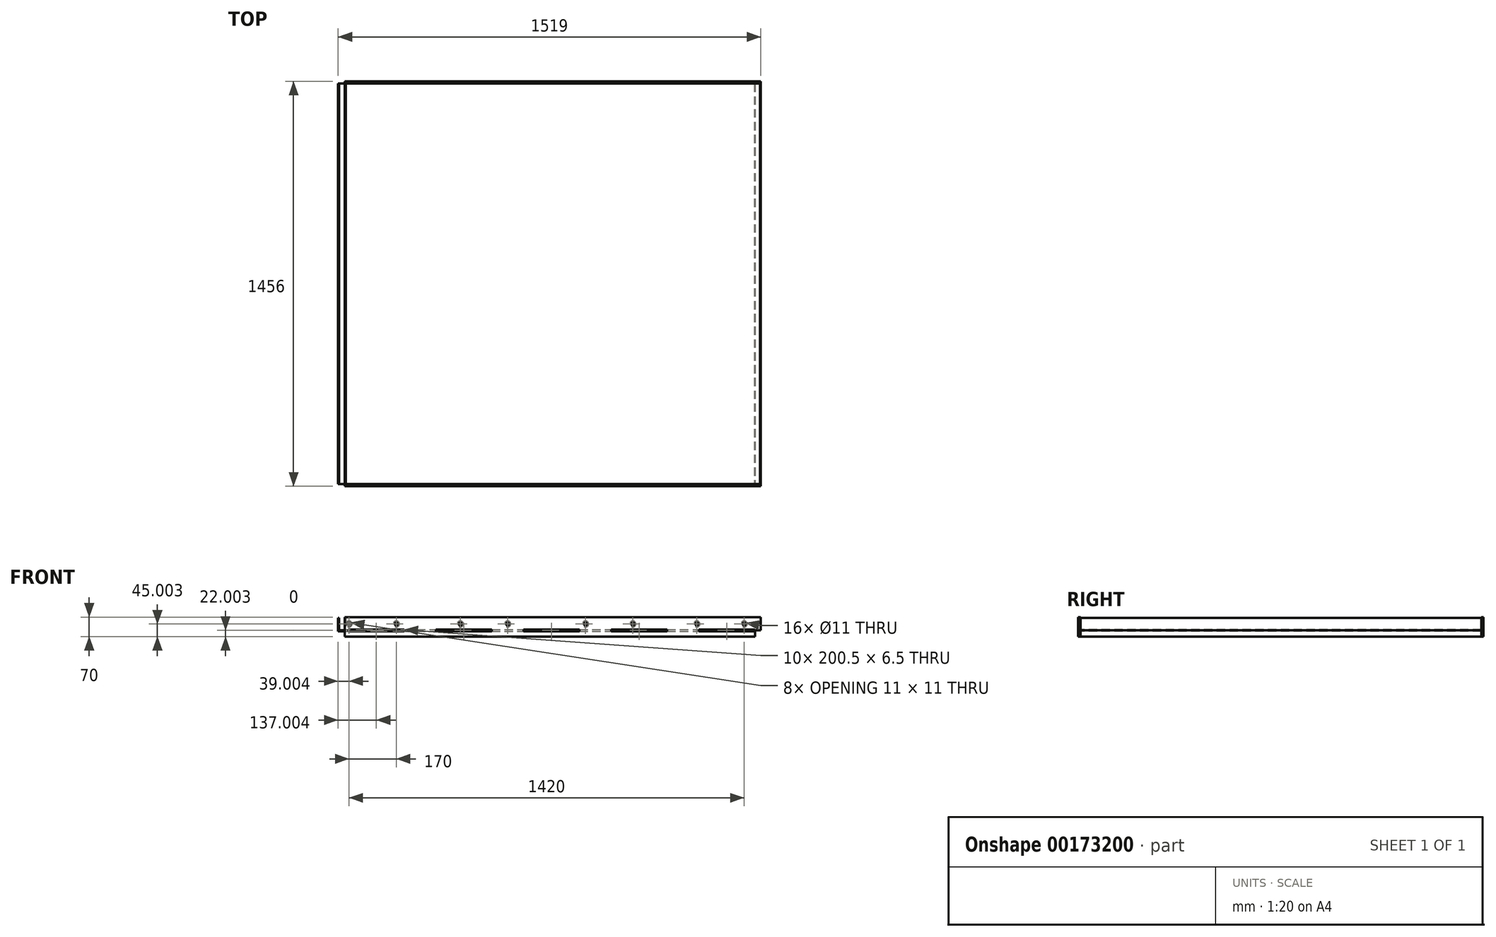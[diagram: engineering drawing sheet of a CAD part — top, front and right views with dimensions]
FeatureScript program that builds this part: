
annotation { "Feature Type Name" : "Feature", "Feature Type Description" : "" }
export const myFeature = defineFeature(function(context is Context, id is Id, definition is map)
    precondition{}
    {
        {
            var Q0;
            Q0=qCreatedBy(makeId("Front.planeOp"),FACE);
            var sketch = newSketch(context, id + "F0", { "sketchPlane" : qUnion([Q0])});
            skLineSegment(sketch, "E0", {"start": v(-1403.49, 88.26) * mm, "end": v(-1403.49, 40.26) * mm});
            skLineSegment(sketch, "E1", {"start": v(-1403.49, 40.26) * mm, "end": v(91.51, 40.26) * mm});
            skLineSegment(sketch, "E2", {"start": v(91.51, 40.26) * mm, "end": v(91.51, 21.26) * mm});
            skLineSegment(sketch, "E3", {"start": v(91.51, 21.26) * mm, "end": v(94.51, 21.26) * mm});
            skLineSegment(sketch, "E4", {"start": v(94.51, 21.26) * mm, "end": v(94.51, 43.26) * mm});
            skLineSegment(sketch, "E5", {"start": v(94.51, 43.26) * mm, "end": v(-1400.49, 43.26) * mm});
            skLineSegment(sketch, "E6", {"start": v(-1400.49, 43.26) * mm, "end": v(-1400.49, 88.26) * mm});
            skLineSegment(sketch, "E7", {"start": v(-1400.49, 88.26) * mm, "end": v(-1403.49, 88.26) * mm});
            skLineSegment(sketch, "E8", {"start": v(-1379.49, 43.26) * mm, "end": v(-1379.49, 88.26) * mm});
            skLineSegment(sketch, "E9", {"start": v(-1379.49, 88.26) * mm, "end": v(-1376.49, 88.26) * mm});
            skLineSegment(sketch, "E10", {"start": v(-1376.49, 88.26) * mm, "end": v(-1376.49, 46.26) * mm});
            skLineSegment(sketch, "E11", {"start": v(-1376.49, 46.26) * mm, "end": v(112.51, 46.26) * mm});
            skLineSegment(sketch, "E12", {"start": v(115.51, 46.26) * mm, "end": v(115.51, 43.26) * mm});
            skLineSegment(sketch, "E13", {"start": v(-1379.49, 43.26) * mm, "end": v(115.51, 43.26) * mm});
            skLineSegment(sketch, "E14", {"start": v(115.51, 46.26) * mm, "end": v(115.51, 88.26) * mm});
            skLineSegment(sketch, "E15", {"start": v(115.51, 88.26) * mm, "end": v(112.51, 88.26) * mm});
            skLineSegment(sketch, "E16", {"start": v(112.51, 88.26) * mm, "end": v(112.51, 46.26) * mm});
            skLineSegment(sketch, "E17.bottom", {"start": v(-1397.49, 82.67) * mm, "end": v(-1382.49, 82.67) * mm, "construction": true});
            skLineSegment(sketch, "E17.top", {"start": v(-1397.49, 47.75) * mm, "end": v(-1382.49, 47.75) * mm, "construction": true});
            skLineSegment(sketch, "E17.left", {"start": v(-1397.49, 82.67) * mm, "end": v(-1397.49, 47.75) * mm, "construction": true});
            skLineSegment(sketch, "E17.right", {"start": v(-1382.49, 82.67) * mm, "end": v(-1382.49, 47.75) * mm, "construction": true});
            skSolve(sketch);
        }
        {
            var Q0;
            Q0=makeQuery(id+"F0.imprint","IMPRINT",FACE,{"disambiguationData":[TD([[makeQuery(id+"F0.imprint","IMPRINT",EDGE,{"derivedFrom":sQuery(id+"F0.wireOp",EDGE,"E0")}),1.0]])]});
            extrude(context, id + "F1", {"entities" : qUnion([Q0]), "oppositeDirection" : true, "depth" : 1440 * mm});
        }
        {
            var Q0;
            {var subQ0=sQuery(id+"F0.wireOp",EDGE,"E8");Q0=makeQuery(id+"F0.imprint","IMPRINT",FACE,{"disambiguationData":[TD([[makeQuery(id+"F0.imprint","IMPRINT",EDGE,{"derivedFrom":subQ0}),-1.0]])]});}
            extrude(context, id + "F2", {"entities" : qUnion([Q0]), "oppositeDirection" : true, "depth" : 1440 * mm});
        }
        {
            var Q0;
            Q0=makeQuery(id+"F1.opExtrude","SWEPT_FACE",FACE,{"disambiguationData":[OSD([sQuery(id+"F0.wireOp",EDGE,"E5"),sQuery(id+"F0.wireOp",EDGE,"E13")])]});
            var sketch = newSketch(context, id + "F3", { "sketchPlane" : qUnion([Q0])});
            skLineSegment(sketch, "E18.bottom", {"start": v(-1366.49, 0) * mm, "end": v(-1166.49, 0) * mm});
            skLineSegment(sketch, "E18.top", {"start": v(-1366.49, -7) * mm, "end": v(-1166.49, -7) * mm});
            skLineSegment(sketch, "E18.left", {"start": v(-1366.49, 0) * mm, "end": v(-1366.49, -7) * mm});
            skLineSegment(sketch, "E18.right", {"start": v(-1166.49, 0) * mm, "end": v(-1166.49, -7) * mm});
            skLineSegment(sketch, "E19.1.0.0", {"start": v(-1051.49, 0) * mm, "end": v(-851.49, 0) * mm});
            skLineSegment(sketch, "E19.1.0.1", {"start": v(-1051.49, -7) * mm, "end": v(-851.49, -7) * mm});
            skLineSegment(sketch, "E19.1.0.2", {"start": v(-851.49, 0) * mm, "end": v(-851.49, -7) * mm});
            skLineSegment(sketch, "E19.1.0.3", {"start": v(-1051.49, 0) * mm, "end": v(-1051.49, -7) * mm});
            skLineSegment(sketch, "E19.2.0.0", {"start": v(-736.49, 0) * mm, "end": v(-536.49, 0) * mm});
            skLineSegment(sketch, "E19.2.0.1", {"start": v(-736.49, -7) * mm, "end": v(-536.49, -7) * mm});
            skLineSegment(sketch, "E19.2.0.2", {"start": v(-536.49, 0) * mm, "end": v(-536.49, -7) * mm});
            skLineSegment(sketch, "E19.2.0.3", {"start": v(-736.49, 0) * mm, "end": v(-736.49, -7) * mm});
            skLineSegment(sketch, "E19.3.0.0", {"start": v(-421.49, 0) * mm, "end": v(-221.49, 0) * mm});
            skLineSegment(sketch, "E19.3.0.1", {"start": v(-421.49, -7) * mm, "end": v(-221.49, -7) * mm});
            skLineSegment(sketch, "E19.3.0.2", {"start": v(-221.49, 0) * mm, "end": v(-221.49, -7) * mm});
            skLineSegment(sketch, "E19.3.0.3", {"start": v(-421.49, 0) * mm, "end": v(-421.49, -7) * mm});
            skLineSegment(sketch, "E19.4.0.0", {"start": v(-106.49, 0) * mm, "end": v(93.51, 0) * mm});
            skLineSegment(sketch, "E19.4.0.1", {"start": v(-106.49, -7) * mm, "end": v(93.51, -7) * mm});
            skLineSegment(sketch, "E19.4.0.2", {"start": v(93.51, 0) * mm, "end": v(93.51, -7) * mm});
            skLineSegment(sketch, "E19.4.0.3", {"start": v(-106.49, 0) * mm, "end": v(-106.49, -7) * mm});
            skLineSegment(sketch, "E19.direction1", {"start": v(-1366.49, -7) * mm, "end": v(-1051.49, -7) * mm, "construction": true});
            skLineSegment(sketch, "E20", {"start": v(-1400.49, 720) * mm, "end": v(412.72, 720) * mm, "construction": true});
            skLineSegment(sketch, "E21.MirrorCS", {"start": v(-1366.49, 1440) * mm, "end": v(-1366.49, 1447) * mm});
            skLineSegment(sketch, "E22.MirrorCS", {"start": v(-1051.49, 1440) * mm, "end": v(-1051.49, 1447) * mm});
            skLineSegment(sketch, "E23.MirrorCS", {"start": v(-421.49, 1440) * mm, "end": v(-421.49, 1447) * mm});
            skLineSegment(sketch, "E24.MirrorCS", {"start": v(93.51, 1440) * mm, "end": v(93.51, 1447) * mm});
            skLineSegment(sketch, "E25.MirrorCS", {"start": v(-221.49, 1440) * mm, "end": v(-221.49, 1447) * mm});
            skLineSegment(sketch, "E26.MirrorCS", {"start": v(-106.49, 1440) * mm, "end": v(-106.49, 1447) * mm});
            skLineSegment(sketch, "E27.MirrorCS", {"start": v(-736.49, 1440) * mm, "end": v(-736.49, 1447) * mm});
            skLineSegment(sketch, "E28.MirrorCS", {"start": v(-536.49, 1440) * mm, "end": v(-536.49, 1447) * mm});
            skLineSegment(sketch, "E29.MirrorCS", {"start": v(-851.49, 1440) * mm, "end": v(-851.49, 1447) * mm});
            skLineSegment(sketch, "E30.MirrorCS", {"start": v(-1166.49, 1440) * mm, "end": v(-1166.49, 1447) * mm});
            skLineSegment(sketch, "E31.MirrorCS", {"start": v(-1366.49, 1440) * mm, "end": v(-1166.49, 1440) * mm});
            skLineSegment(sketch, "E32.MirrorCS", {"start": v(-106.49, 1447) * mm, "end": v(93.51, 1447) * mm});
            skLineSegment(sketch, "E33.MirrorCS", {"start": v(-421.49, 1440) * mm, "end": v(-221.49, 1440) * mm});
            skLineSegment(sketch, "E34.MirrorCS", {"start": v(-736.49, 1440) * mm, "end": v(-536.49, 1440) * mm});
            skLineSegment(sketch, "E35.MirrorCS", {"start": v(-1366.49, 1447) * mm, "end": v(-1166.49, 1447) * mm});
            skLineSegment(sketch, "E36.MirrorCS", {"start": v(-1051.49, 1440) * mm, "end": v(-851.49, 1440) * mm});
            skLineSegment(sketch, "E37.MirrorCS", {"start": v(-106.49, 1440) * mm, "end": v(93.51, 1440) * mm});
            skLineSegment(sketch, "E38.MirrorCS", {"start": v(-421.49, 1447) * mm, "end": v(-221.49, 1447) * mm});
            skLineSegment(sketch, "E39.MirrorCS", {"start": v(-1366.49, 1447) * mm, "end": v(-1051.49, 1447) * mm, "construction": true});
            skLineSegment(sketch, "E40.MirrorCS", {"start": v(-736.49, 1447) * mm, "end": v(-536.49, 1447) * mm});
            skLineSegment(sketch, "E41.MirrorCS", {"start": v(-1051.49, 1447) * mm, "end": v(-851.49, 1447) * mm});
            skSolve(sketch);
        }
        {
            var Q0;
            Q0=qSketchRegion(id+"F3",true);
            extrude(context, id + "F4", {"entities" : qUnion([Q0]), "operationType" : NewBodyOperationType.ADD, "oppositeDirection" : true, "depth" : 3 * mm});
        }
        {
            var Q0;
            Q0=makeQuery(id+"F2.opExtrude","SWEPT_FACE",FACE,{"disambiguationData":[OSD([sQuery(id+"F0.wireOp",EDGE,"E11")])]});
            var sketch = newSketch(context, id + "F5", { "sketchPlane" : qUnion([Q0])});
            skLineSegment(sketch, "E42.bottom", {"start": v(-1366.49, 0) * mm, "end": v(-1166.49, 0) * mm});
            skLineSegment(sketch, "E42.top", {"start": v(-1366.49, -7) * mm, "end": v(-1166.49, -7) * mm});
            skLineSegment(sketch, "E42.left", {"start": v(-1366.49, 0) * mm, "end": v(-1366.49, -7) * mm});
            skLineSegment(sketch, "E42.right", {"start": v(-1166.49, 0) * mm, "end": v(-1166.49, -7) * mm});
            skLineSegment(sketch, "E43.1.0.0", {"start": v(-1051.49, -7) * mm, "end": v(-851.49, -7) * mm});
            skLineSegment(sketch, "E43.1.0.1", {"start": v(-1051.49, 0) * mm, "end": v(-851.49, 0) * mm});
            skLineSegment(sketch, "E43.1.0.2", {"start": v(-1051.49, 0) * mm, "end": v(-1051.49, -7) * mm});
            skLineSegment(sketch, "E43.1.0.3", {"start": v(-851.49, 0) * mm, "end": v(-851.49, -7) * mm});
            skLineSegment(sketch, "E43.2.0.0", {"start": v(-736.49, -7) * mm, "end": v(-536.49, -7) * mm});
            skLineSegment(sketch, "E43.2.0.1", {"start": v(-736.49, 0) * mm, "end": v(-536.49, 0) * mm});
            skLineSegment(sketch, "E43.2.0.2", {"start": v(-736.49, 0) * mm, "end": v(-736.49, -7) * mm});
            skLineSegment(sketch, "E43.2.0.3", {"start": v(-536.49, 0) * mm, "end": v(-536.49, -7) * mm});
            skLineSegment(sketch, "E43.3.0.0", {"start": v(-421.49, -7) * mm, "end": v(-221.49, -7) * mm});
            skLineSegment(sketch, "E43.3.0.1", {"start": v(-421.49, 0) * mm, "end": v(-221.49, 0) * mm});
            skLineSegment(sketch, "E43.3.0.2", {"start": v(-421.49, 0) * mm, "end": v(-421.49, -7) * mm});
            skLineSegment(sketch, "E43.3.0.3", {"start": v(-221.49, 0) * mm, "end": v(-221.49, -7) * mm});
            skLineSegment(sketch, "E43.4.0.0", {"start": v(-106.49, -7) * mm, "end": v(93.51, -7) * mm});
            skLineSegment(sketch, "E43.4.0.1", {"start": v(-106.49, 0) * mm, "end": v(93.51, 0) * mm});
            skLineSegment(sketch, "E43.4.0.2", {"start": v(-106.49, 0) * mm, "end": v(-106.49, -7) * mm});
            skLineSegment(sketch, "E43.4.0.3", {"start": v(93.51, 0) * mm, "end": v(93.51, -7) * mm});
            skLineSegment(sketch, "E43.direction1", {"start": v(-1366.49, -7) * mm, "end": v(-1051.49, -7) * mm, "construction": true});
            skLineSegment(sketch, "E44", {"start": v(-1376.49, 720) * mm, "end": v(410.62, 720) * mm, "construction": true});
            skPoint(sketch, "E44.endSnap0", {"position": v(112.51, 720) * mm});
            skLineSegment(sketch, "E45.MirrorCS", {"start": v(-1051.49, 1440) * mm, "end": v(-1051.49, 1447) * mm});
            skLineSegment(sketch, "E46.MirrorCS", {"start": v(-1366.49, 1440) * mm, "end": v(-1366.49, 1447) * mm});
            skLineSegment(sketch, "E47.MirrorCS", {"start": v(-106.49, 1440) * mm, "end": v(-106.49, 1447) * mm});
            skLineSegment(sketch, "E48.MirrorCS", {"start": v(-536.49, 1440) * mm, "end": v(-536.49, 1447) * mm});
            skLineSegment(sketch, "E49.MirrorCS", {"start": v(-736.49, 1440) * mm, "end": v(-736.49, 1447) * mm});
            skLineSegment(sketch, "E50.MirrorCS", {"start": v(-851.49, 1440) * mm, "end": v(-851.49, 1447) * mm});
            skLineSegment(sketch, "E51.MirrorCS", {"start": v(-1166.49, 1440) * mm, "end": v(-1166.49, 1447) * mm});
            skLineSegment(sketch, "E52.MirrorCS", {"start": v(93.51, 1440) * mm, "end": v(93.51, 1447) * mm});
            skLineSegment(sketch, "E53.MirrorCS", {"start": v(-221.49, 1440) * mm, "end": v(-221.49, 1447) * mm});
            skLineSegment(sketch, "E54.MirrorCS", {"start": v(-421.49, 1440) * mm, "end": v(-421.49, 1447) * mm});
            skLineSegment(sketch, "E55.MirrorCS", {"start": v(-1366.49, 1447) * mm, "end": v(-1166.49, 1447) * mm});
            skLineSegment(sketch, "E56.MirrorCS", {"start": v(-1366.49, 1447) * mm, "end": v(-1051.49, 1447) * mm, "construction": true});
            skLineSegment(sketch, "E57.MirrorCS", {"start": v(-106.49, 1447) * mm, "end": v(93.51, 1447) * mm});
            skLineSegment(sketch, "E58.MirrorCS", {"start": v(-421.49, 1447) * mm, "end": v(-221.49, 1447) * mm});
            skLineSegment(sketch, "E59.MirrorCS", {"start": v(-736.49, 1440) * mm, "end": v(-536.49, 1440) * mm});
            skLineSegment(sketch, "E60.MirrorCS", {"start": v(-736.49, 1447) * mm, "end": v(-536.49, 1447) * mm});
            skLineSegment(sketch, "E61.MirrorCS", {"start": v(-1051.49, 1440) * mm, "end": v(-851.49, 1440) * mm});
            skLineSegment(sketch, "E62.MirrorCS", {"start": v(-1051.49, 1447) * mm, "end": v(-851.49, 1447) * mm});
            skLineSegment(sketch, "E63.MirrorCS", {"start": v(-1366.49, 1440) * mm, "end": v(-1166.49, 1440) * mm});
            skLineSegment(sketch, "E64.MirrorCS", {"start": v(-106.49, 1440) * mm, "end": v(93.51, 1440) * mm});
            skLineSegment(sketch, "E65.MirrorCS", {"start": v(-421.49, 1440) * mm, "end": v(-221.49, 1440) * mm});
            skSolve(sketch);
        }
        {
            var Q0;
            Q0=qSketchRegion(id+"F5",true);
            extrude(context, id + "F6", {"entities" : qUnion([Q0]), "operationType" : NewBodyOperationType.ADD, "oppositeDirection" : true, "depth" : 3 * mm});
        }
        {
            var Q0;
            {var subQ20=sQuery(id+"F0.wireOp",EDGE,"E1");var subQ29=sQuery(id+"F0.wireOp",EDGE,"E6");var subQ34=sQuery(id+"F0.wireOp",EDGE,"E0");var subQ35=sQuery(id+"F0.wireOp",EDGE,"E7");var subQ40=sQuery(id+"F0.wireOp",EDGE,"E13");var subQ41=sQuery(id+"F0.wireOp",EDGE,"E5");Q0=makeQuery(id+"F4.boolean.opBoolean","SPLIT",FACE,{"disambiguationData":[TD([makeQuery(id+"F1.opExtrude","SWEPT_FACE",FACE,{"disambiguationData":[OSD([subQ34])]})])],"derivedFrom":makeQuery(id+"F1.opExtrude","CAP_FACE",FACE,{"disambiguationData":[OSD([subQ34,subQ20,sQuery(id+"F0.wireOp",EDGE,"E2"),sQuery(id+"F0.wireOp",EDGE,"E3"),sQuery(id+"F0.wireOp",EDGE,"E4"),subQ41,subQ29,subQ35,subQ40])],"isStart":true})});}
            var sketch = newSketch(context, id + "F7", { "sketchPlane" : qUnion([Q0])});
            skLineSegment(sketch, "E66", {"start": v(115.51, 43.26) * mm, "end": v(94.51, 43.26) * mm});
            skLineSegment(sketch, "E67", {"start": v(94.51, 43.26) * mm, "end": v(94.51, 21.26) * mm});
            skLineSegment(sketch, "E68", {"start": v(94.51, 21.26) * mm, "end": v(-1379.49, 21.26) * mm});
            skLineSegment(sketch, "E69", {"start": v(-1379.49, 21.26) * mm, "end": v(-1379.49, 91.26) * mm});
            skLineSegment(sketch, "E70", {"start": v(-1379.49, 91.26) * mm, "end": v(115.51, 91.26) * mm});
            skLineSegment(sketch, "E71", {"start": v(115.51, 91.26) * mm, "end": v(115.51, 43.26) * mm});
            skLineSegment(sketch, "E72.bottom", {"start": v(-1366.74, 46.51) * mm, "end": v(-1166.24, 46.51) * mm});
            skLineSegment(sketch, "E72.top", {"start": v(-1366.74, 40.01) * mm, "end": v(-1166.24, 40.01) * mm});
            skLineSegment(sketch, "E72.left", {"start": v(-1366.74, 46.51) * mm, "end": v(-1366.74, 40.01) * mm});
            skLineSegment(sketch, "E72.right", {"start": v(-1166.24, 46.51) * mm, "end": v(-1166.24, 40.01) * mm});
            skLineSegment(sketch, "E73.1.0.0", {"start": v(-1051.74, 46.51) * mm, "end": v(-851.24, 46.51) * mm});
            skLineSegment(sketch, "E73.1.0.1", {"start": v(-1051.74, 40.01) * mm, "end": v(-851.24, 40.01) * mm});
            skLineSegment(sketch, "E73.1.0.2", {"start": v(-1051.74, 46.51) * mm, "end": v(-1051.74, 40.01) * mm});
            skLineSegment(sketch, "E73.1.0.3", {"start": v(-851.24, 46.51) * mm, "end": v(-851.24, 40.01) * mm});
            skLineSegment(sketch, "E73.2.0.0", {"start": v(-736.74, 46.51) * mm, "end": v(-536.24, 46.51) * mm});
            skLineSegment(sketch, "E73.2.0.1", {"start": v(-736.74, 40.01) * mm, "end": v(-536.24, 40.01) * mm});
            skLineSegment(sketch, "E73.2.0.2", {"start": v(-736.74, 46.51) * mm, "end": v(-736.74, 40.01) * mm});
            skLineSegment(sketch, "E73.2.0.3", {"start": v(-536.24, 46.51) * mm, "end": v(-536.24, 40.01) * mm});
            skLineSegment(sketch, "E73.3.0.0", {"start": v(-421.74, 46.51) * mm, "end": v(-221.24, 46.51) * mm});
            skLineSegment(sketch, "E73.3.0.1", {"start": v(-421.74, 40.01) * mm, "end": v(-221.24, 40.01) * mm});
            skLineSegment(sketch, "E73.3.0.2", {"start": v(-421.74, 46.51) * mm, "end": v(-421.74, 40.01) * mm});
            skLineSegment(sketch, "E73.3.0.3", {"start": v(-221.24, 46.51) * mm, "end": v(-221.24, 40.01) * mm});
            skLineSegment(sketch, "E73.4.0.0", {"start": v(-106.74, 46.51) * mm, "end": v(93.76, 46.51) * mm});
            skLineSegment(sketch, "E73.4.0.1", {"start": v(-106.74, 40.01) * mm, "end": v(93.76, 40.01) * mm});
            skLineSegment(sketch, "E73.4.0.2", {"start": v(-106.74, 46.51) * mm, "end": v(-106.74, 40.01) * mm});
            skLineSegment(sketch, "E73.4.0.3", {"start": v(93.76, 46.51) * mm, "end": v(93.76, 40.01) * mm});
            skLineSegment(sketch, "E73.direction1", {"start": v(-1366.74, 40.01) * mm, "end": v(-1051.74, 40.01) * mm, "construction": true});
            skSolve(sketch);
        }
        {
            var Q0;
            Q0=qSketchRegion(id+"F7",true);
            extrude(context, id + "F8", {"entities" : qUnion([Q0]), "depth" : 8 * mm});
        }
        {
            var Q0;
            Q0=sQuery(id+"F5.wireOp",EDGE,"E44");
            cPlane(context, id + "F9", {"entities" : qUnion([Q0]), "cplaneType" : CPlaneType.LINE_ANGLE, "offset" : 25 * mm, "angle" : 0 * degree, "width" : 150 * mm, "height" : 150 * mm});
        }
        {
            var Q0;
            Q0=makeQuery(id+"F8.opExtrude","CAP_FACE",FACE,{"disambiguationData":[OSD([sQuery(id+"F7.wireOp",EDGE,"E66"),sQuery(id+"F7.wireOp",EDGE,"E67"),sQuery(id+"F7.wireOp",EDGE,"E68"),sQuery(id+"F7.wireOp",EDGE,"E69"),sQuery(id+"F7.wireOp",EDGE,"E70"),sQuery(id+"F7.wireOp",EDGE,"E71"),sQuery(id+"F7.wireOp",EDGE,"E72.bottom"),sQuery(id+"F7.wireOp",EDGE,"E72.top"),sQuery(id+"F7.wireOp",EDGE,"E72.left"),sQuery(id+"F7.wireOp",EDGE,"E72.right"),sQuery(id+"F7.wireOp",EDGE,"E73.1.0.0"),sQuery(id+"F7.wireOp",EDGE,"E73.1.0.1"),sQuery(id+"F7.wireOp",EDGE,"E73.1.0.2"),sQuery(id+"F7.wireOp",EDGE,"E73.1.0.3"),sQuery(id+"F7.wireOp",EDGE,"E73.2.0.0"),sQuery(id+"F7.wireOp",EDGE,"E73.2.0.1"),sQuery(id+"F7.wireOp",EDGE,"E73.2.0.2"),sQuery(id+"F7.wireOp",EDGE,"E73.2.0.3"),sQuery(id+"F7.wireOp",EDGE,"E73.3.0.0"),sQuery(id+"F7.wireOp",EDGE,"E73.3.0.1"),sQuery(id+"F7.wireOp",EDGE,"E73.3.0.2"),sQuery(id+"F7.wireOp",EDGE,"E73.3.0.3"),sQuery(id+"F7.wireOp",EDGE,"E73.4.0.0"),sQuery(id+"F7.wireOp",EDGE,"E73.4.0.1"),sQuery(id+"F7.wireOp",EDGE,"E73.4.0.2"),sQuery(id+"F7.wireOp",EDGE,"E73.4.0.3")])],"isStart":true});
            var sketch = newSketch(context, id + "F10", { "sketchPlane" : qUnion([Q0])});
            skPoint(sketch, "E74", {"position": v(-55.51, 66.26) * mm});
            skPoint(sketch, "E75", {"position": v(114.49, 66.26) * mm});
            skPoint(sketch, "E76", {"position": v(344.49, 66.26) * mm});
            skPoint(sketch, "E77", {"position": v(514.49, 66.26) * mm});
            skPoint(sketch, "E78", {"position": v(794.49, 66.26) * mm});
            skPoint(sketch, "E79", {"position": v(964.49, 66.26) * mm});
            skPoint(sketch, "E80", {"position": v(1194.49, 66.26) * mm});
            skPoint(sketch, "E81", {"position": v(1364.49, 66.26) * mm});
            skSolve(sketch);
        }
        {
            var Q0;
            Q0=sQuery(id+"F10.wireOp",VERTEX,"E81");
            var Q1;
            Q1=sQuery(id+"F10.wireOp",VERTEX,"E80");
            var Q2;
            Q2=sQuery(id+"F10.wireOp",VERTEX,"E79");
            var Q3;
            Q3=sQuery(id+"F10.wireOp",VERTEX,"E78");
            var Q4;
            Q4=sQuery(id+"F10.wireOp",VERTEX,"E77");
            var Q5;
            Q5=sQuery(id+"F10.wireOp",VERTEX,"E76");
            var Q6;
            Q6=sQuery(id+"F10.wireOp",VERTEX,"E75");
            var Q7;
            Q7=sQuery(id+"F10.wireOp",VERTEX,"E74");
            var Q8;
            Q8=makeQuery(id+"F8.opExtrude","SWEPT_BODY",BODY,{"disambiguationData":[OSD([sQuery(id+"F7.wireOp",EDGE,"E66"),sQuery(id+"F7.wireOp",EDGE,"E67"),sQuery(id+"F7.wireOp",EDGE,"E68"),sQuery(id+"F7.wireOp",EDGE,"E69"),sQuery(id+"F7.wireOp",EDGE,"E70"),sQuery(id+"F7.wireOp",EDGE,"E71"),sQuery(id+"F7.wireOp",EDGE,"E72.bottom"),sQuery(id+"F7.wireOp",EDGE,"E72.top"),sQuery(id+"F7.wireOp",EDGE,"E72.left"),sQuery(id+"F7.wireOp",EDGE,"E72.right"),sQuery(id+"F7.wireOp",EDGE,"E73.1.0.0"),sQuery(id+"F7.wireOp",EDGE,"E73.1.0.1"),sQuery(id+"F7.wireOp",EDGE,"E73.1.0.2"),sQuery(id+"F7.wireOp",EDGE,"E73.1.0.3"),sQuery(id+"F7.wireOp",EDGE,"E73.2.0.0"),sQuery(id+"F7.wireOp",EDGE,"E73.2.0.1"),sQuery(id+"F7.wireOp",EDGE,"E73.2.0.2"),sQuery(id+"F7.wireOp",EDGE,"E73.2.0.3"),sQuery(id+"F7.wireOp",EDGE,"E73.3.0.0"),sQuery(id+"F7.wireOp",EDGE,"E73.3.0.1"),sQuery(id+"F7.wireOp",EDGE,"E73.3.0.2"),sQuery(id+"F7.wireOp",EDGE,"E73.3.0.3"),sQuery(id+"F7.wireOp",EDGE,"E73.4.0.0"),sQuery(id+"F7.wireOp",EDGE,"E73.4.0.1"),sQuery(id+"F7.wireOp",EDGE,"E73.4.0.2"),sQuery(id+"F7.wireOp",EDGE,"E73.4.0.3")])]});
            hole(context, id + "F11", {"style" : HoleStyle.C_SINK, "endStyle" : HoleEndStyle.THROUGH, "holeDiameter" : 11 * mm, "cSinkDiameter" : 22 * mm, "cSinkAngle" : 90 * degree, "locations" : qUnion([Q0, Q1, Q2, Q3, Q4, Q5, Q6, Q7]), "scope" : qUnion([Q8]), "isTappedThrough" : true});
        }
        {
            var Q0;
            Q0=makeQuery(id+"F8.opExtrude","SWEPT_BODY",BODY,{"disambiguationData":[OSD([sQuery(id+"F7.wireOp",EDGE,"E66"),sQuery(id+"F7.wireOp",EDGE,"E67"),sQuery(id+"F7.wireOp",EDGE,"E68"),sQuery(id+"F7.wireOp",EDGE,"E69"),sQuery(id+"F7.wireOp",EDGE,"E70"),sQuery(id+"F7.wireOp",EDGE,"E71"),sQuery(id+"F7.wireOp",EDGE,"E72.bottom"),sQuery(id+"F7.wireOp",EDGE,"E72.top"),sQuery(id+"F7.wireOp",EDGE,"E72.left"),sQuery(id+"F7.wireOp",EDGE,"E72.right"),sQuery(id+"F7.wireOp",EDGE,"E73.1.0.0"),sQuery(id+"F7.wireOp",EDGE,"E73.1.0.1"),sQuery(id+"F7.wireOp",EDGE,"E73.1.0.2"),sQuery(id+"F7.wireOp",EDGE,"E73.1.0.3"),sQuery(id+"F7.wireOp",EDGE,"E73.2.0.0"),sQuery(id+"F7.wireOp",EDGE,"E73.2.0.1"),sQuery(id+"F7.wireOp",EDGE,"E73.2.0.2"),sQuery(id+"F7.wireOp",EDGE,"E73.2.0.3"),sQuery(id+"F7.wireOp",EDGE,"E73.3.0.0"),sQuery(id+"F7.wireOp",EDGE,"E73.3.0.1"),sQuery(id+"F7.wireOp",EDGE,"E73.3.0.2"),sQuery(id+"F7.wireOp",EDGE,"E73.3.0.3"),sQuery(id+"F7.wireOp",EDGE,"E73.4.0.0"),sQuery(id+"F7.wireOp",EDGE,"E73.4.0.1"),sQuery(id+"F7.wireOp",EDGE,"E73.4.0.2"),sQuery(id+"F7.wireOp",EDGE,"E73.4.0.3")])]});
            var Q1;
            Q1=qCreatedBy(id+"F9.planeOp",FACE);
            mirror(context, id + "F12", {"entities" : qUnion([Q0]), "mirrorPlane" : qUnion([Q1])});
        }
    });
